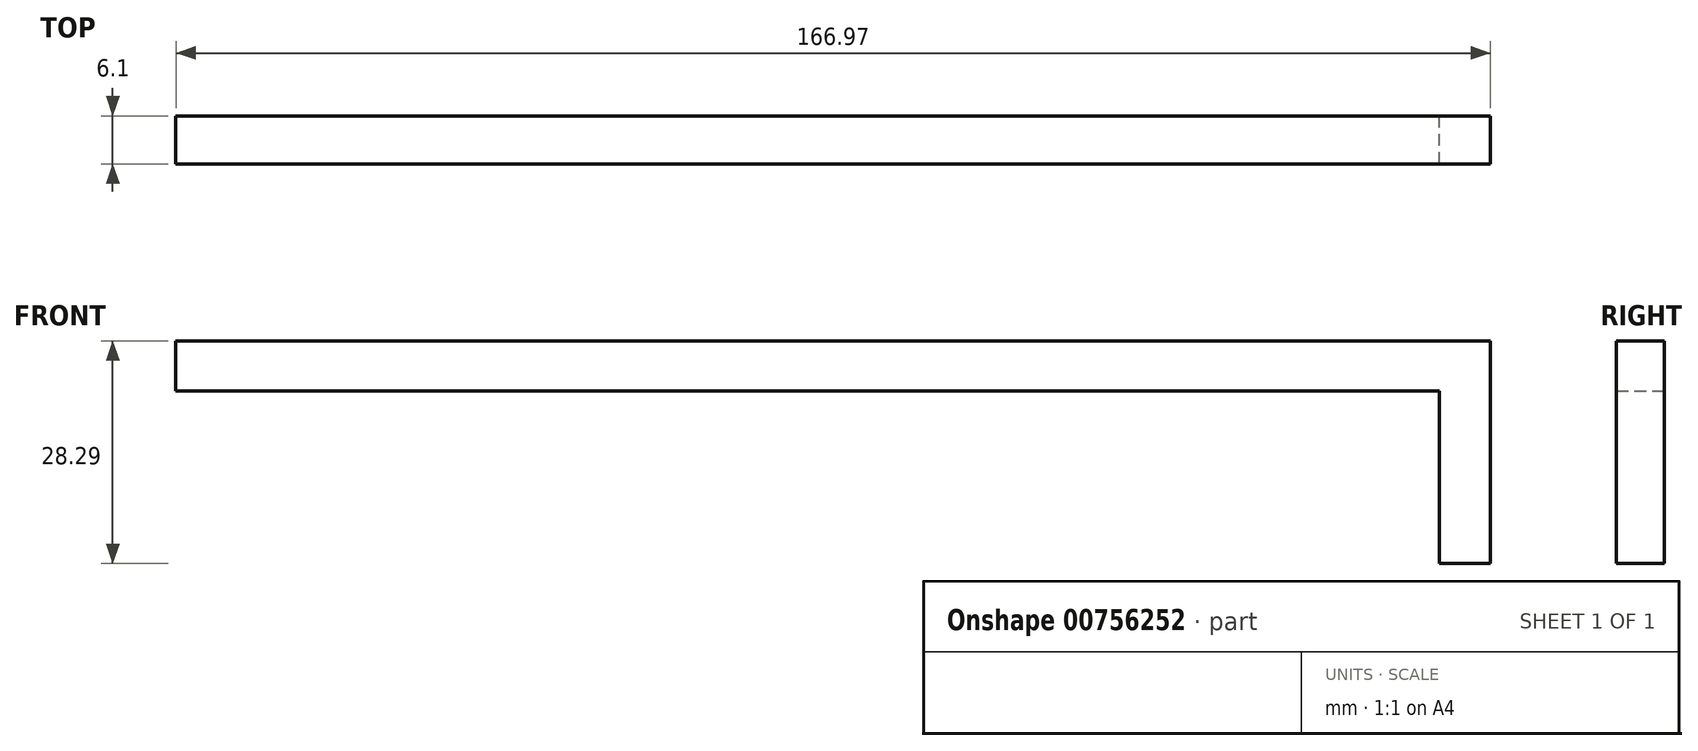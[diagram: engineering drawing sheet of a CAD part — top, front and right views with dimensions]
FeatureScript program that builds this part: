
annotation { "Feature Type Name" : "Feature", "Feature Type Description" : "" }
export const myFeature = defineFeature(function(context is Context, id is Id, definition is map)
    precondition{}
    {
        {
            var Q0;
            Q0=qCreatedBy(makeId("Front.planeOp"),FACE);
            var sketch = newSketch(context, id + "F0", { "sketchPlane" : qUnion([Q0])});
            skLineSegment(sketch, "E0", {"start": v(-82.6, 0) * mm, "end": v(84.38, 0) * mm});
            skLineSegment(sketch, "E1", {"start": v(-82.6, 0) * mm, "end": v(-82.6, -6.35) * mm});
            skLineSegment(sketch, "E2", {"start": v(-82.6, -6.35) * mm, "end": v(77.94, -6.35) * mm});
            skLineSegment(sketch, "E3", {"start": v(84.38, 0) * mm, "end": v(84.38, -28.29) * mm});
            skLineSegment(sketch, "E4", {"start": v(77.94, -6.35) * mm, "end": v(77.94, -28.29) * mm});
            skLineSegment(sketch, "E5", {"start": v(77.94, -28.29) * mm, "end": v(84.38, -28.29) * mm});
            skSolve(sketch);
        }
        {
            var Q0;
            Q0 = qSketchRegion(id + "F0", true);
            extrude(context, id + "F1", {"entities" : qUnion([Q0]), "endBound" : BoundingType.SYMMETRIC, "depth" : 6.1 * mm, "offsetDistance" : 25.4 * mm});
        }
    });
